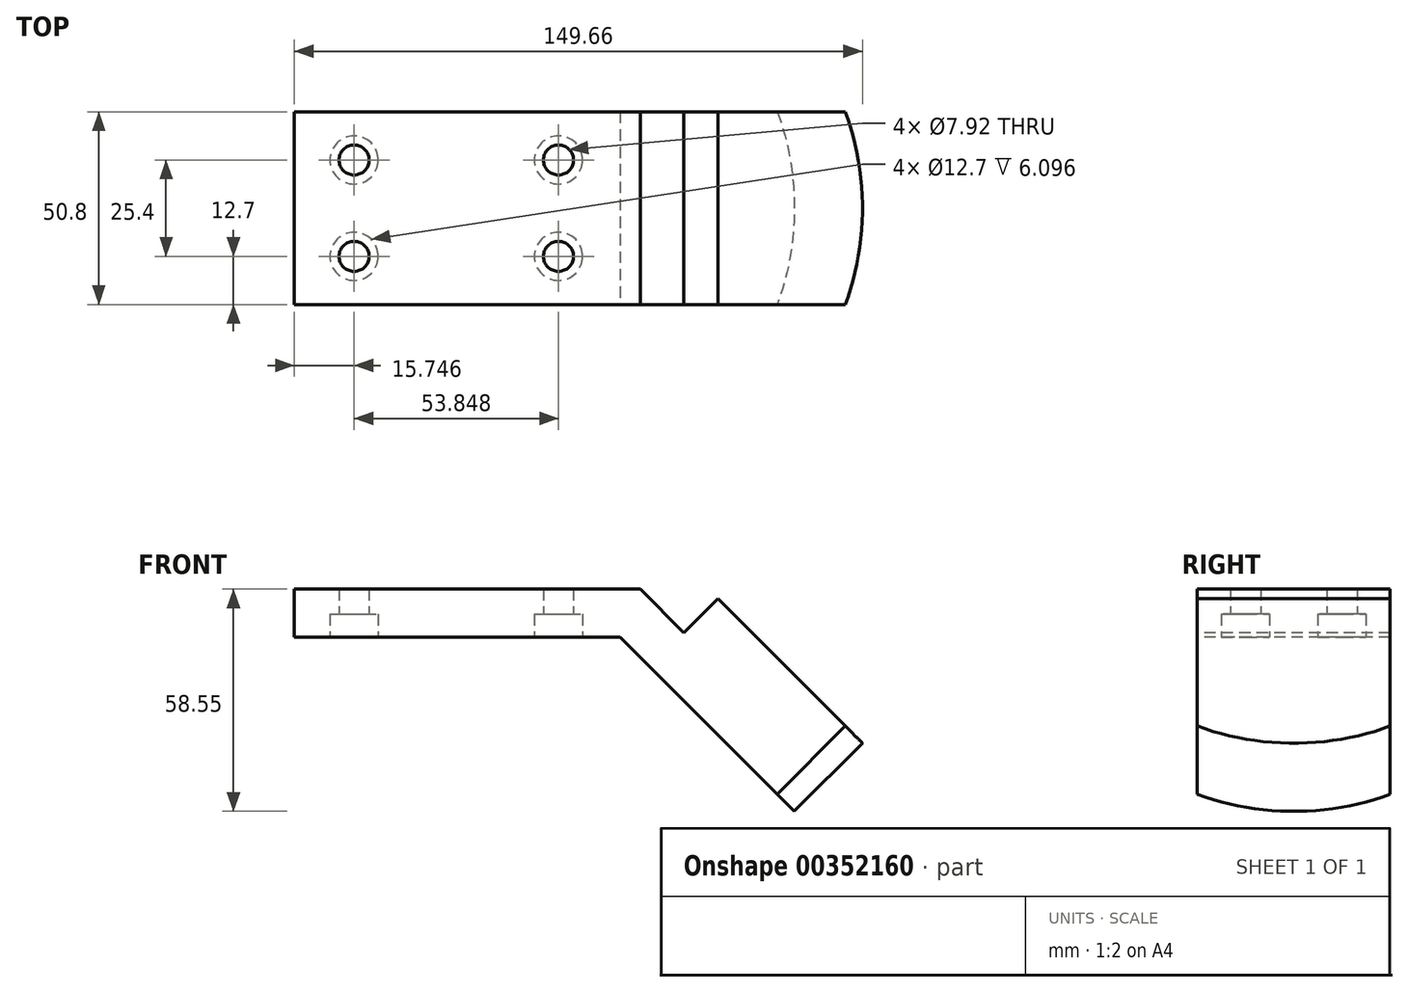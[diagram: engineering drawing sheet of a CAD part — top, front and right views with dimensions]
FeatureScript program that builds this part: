
annotation { "Feature Type Name" : "Feature", "Feature Type Description" : "" }
export const myFeature = defineFeature(function(context is Context, id is Id, definition is map)
    precondition{}
    {
        {
            var Q0;
            Q0=qCreatedBy(makeId("Front.planeOp"),FACE);
            var sketch = newSketch(context, id + "F0", { "sketchPlane" : qUnion([Q0])});
            skLineSegment(sketch, "E0", {"start": v(-17.57, 2.51) * mm, "end": v(-17.57, -10.19) * mm});
            skLineSegment(sketch, "E1", {"start": v(-17.57, -10.19) * mm, "end": v(68.28, -10.19) * mm});
            skLineSegment(sketch, "E2", {"start": v(68.28, -10.19) * mm, "end": v(114.13, -56.04) * mm});
            skLineSegment(sketch, "E3", {"start": v(114.13, -56.04) * mm, "end": v(132.1, -38.08) * mm});
            skLineSegment(sketch, "E4", {"start": v(132.1, -38.08) * mm, "end": v(94.02, 0) * mm});
            skLineSegment(sketch, "E5", {"start": v(94.02, 0) * mm, "end": v(85.04, -8.98) * mm});
            skLineSegment(sketch, "E6", {"start": v(85.04, -8.98) * mm, "end": v(73.54, 2.51) * mm});
            skLineSegment(sketch, "E7", {"start": v(73.54, 2.51) * mm, "end": v(-17.57, 2.51) * mm});
            skSolve(sketch);
        }
        {
            var Q0;
            Q0 = qSketchRegion(id + "F0", true);
            extrude(context, id + "F1", {"entities" : qUnion([Q0]), "oppositeDirection" : true, "depth" : 50.8 * mm});
        }
        {
            var Q0;
            Q0=makeQuery(id+"F1.opExtrude","SWEPT_FACE",FACE,{"disambiguationData":[OSD([sQuery(id+"F0.wireOp",EDGE,"E1")])]});
            cPlane(context, id + "F2", {"entities" : qUnion([Q0]), "cplaneType" : CPlaneType.OFFSET, "offset" : 0 * mm, "width" : 152.4 * mm, "height" : 152.4 * mm});
        }
        {
            var Q0;
            Q0=qCreatedBy(id+"F2.planeOp",FACE);
            var sketch = newSketch(context, id + "F3", { "sketchPlane" : qUnion([Q0])});
            skCircle(sketch, "E8", {"center": v(-1.82, -12.7) * mm, "radius": 3.96 * mm});
            skCircle(sketch, "E9", {"center": v(-1.82, -38.1) * mm, "radius": 3.96 * mm});
            skCircle(sketch, "E10", {"center": v(52.02, -12.7) * mm, "radius": 3.96 * mm});
            skCircle(sketch, "E11", {"center": v(52.02, -38.1) * mm, "radius": 3.96 * mm});
            skSolve(sketch);
        }
        {
            var Q0;
            Q0=sQuery(id+"F3.wireOp",VERTEX,"E8.center");
            var Q1;
            Q1=sQuery(id+"F3.wireOp",VERTEX,"E9.center");
            var Q2;
            Q2=sQuery(id+"F3.wireOp",VERTEX,"E10.center");
            var Q3;
            Q3=sQuery(id+"F3.wireOp",VERTEX,"E11.center");
            var Q4;
            Q4=makeQuery(id+"F1.opExtrude","SWEPT_BODY",BODY,{"disambiguationData":[OSD([sQuery(id+"F0.wireOp",EDGE,"E0"),sQuery(id+"F0.wireOp",EDGE,"E1"),sQuery(id+"F0.wireOp",EDGE,"E2"),sQuery(id+"F0.wireOp",EDGE,"E3"),sQuery(id+"F0.wireOp",EDGE,"E4"),sQuery(id+"F0.wireOp",EDGE,"E5"),sQuery(id+"F0.wireOp",EDGE,"E6"),sQuery(id+"F0.wireOp",EDGE,"E7")])]});
            hole(context, id + "F4", {"style" : HoleStyle.C_BORE, "endStyle" : HoleEndStyle.THROUGH, "holeDiameter" : 7.92 * mm, "cBoreDiameter" : 12.7 * mm, "cBoreDepth" : 6.1 * mm, "isTappedThrough" : true, "tappedDepth" : 12.7 * mm, "tapClearance" : 3, "startFromSketch" : true, "locations" : qUnion([Q0, Q1, Q2, Q3]), "scope" : qUnion([Q4])});
        }
        {
            var Q0;
            Q0=makeQuery(id+"F1.opExtrude","SWEPT_FACE",FACE,{"disambiguationData":[OSD([sQuery(id+"F0.wireOp",EDGE,"E4")])]});
            cPlane(context, id + "F5", {"entities" : qUnion([Q0]), "cplaneType" : CPlaneType.OFFSET, "offset" : 0 * mm, "width" : 152.4 * mm, "height" : 152.4 * mm});
        }
        {
            var Q0;
            Q0=makeQuery(id+"F1.opExtrude","SWEPT_FACE",FACE,{"disambiguationData":[OSD([sQuery(id+"F0.wireOp",EDGE,"E3")])]});
            cPlane(context, id + "F6", {"entities" : qUnion([Q0]), "cplaneType" : CPlaneType.OFFSET, "offset" : 0 * mm, "width" : 152.4 * mm, "height" : 152.4 * mm});
        }
        {
            var Q0;
            Q0=qCreatedBy(id+"F5.planeOp",FACE);
            var sketch = newSketch(context, id + "F7", { "sketchPlane" : qUnion([Q0])});
            skArc(sketch, "E12", {"start": v(0, -113.96) * mm, "mid": v(25.4, -120.33) * mm, "end": v(50.8, -113.96) * mm});
            skLineSegment(sketch, "E13", {"start": v(0, -113.96) * mm, "end": v(0, -123.43) * mm});
            skLineSegment(sketch, "E14", {"start": v(0, -123.43) * mm, "end": v(50.8, -123.43) * mm});
            skLineSegment(sketch, "E15", {"start": v(50.8, -123.43) * mm, "end": v(50.8, -113.96) * mm});
            skSolve(sketch);
        }
        {
            var Q0;
            Q0 = qSketchRegion(id + "F7", true);
            extrude(context, id + "F8", {"entities" : qUnion([Q0]), "operationType" : NewBodyOperationType.REMOVE, "endBound" : BoundingType.THROUGH_ALL, "oppositeDirection" : true, "depth" : 25.4 * mm});
        }
        {
            var Q0;
            Q0=qCreatedBy(id+"F6.planeOp",FACE);
            var sketch = newSketch(context, id + "F9", { "sketchPlane" : qUnion([Q0])});
            skLineSegment(sketch, "E16", {"start": v(66.48, -15.75) * mm, "end": v(60.38, -15.75) * mm});
            skLineSegment(sketch, "E17", {"start": v(60.38, -15.75) * mm, "end": v(60.38, -9.65) * mm});
            skLineSegment(sketch, "E18", {"start": v(60.38, -9.65) * mm, "end": v(53.78, -9.65) * mm});
            skLineSegment(sketch, "E19", {"start": v(53.78, -9.65) * mm, "end": v(53.78, -41.15) * mm});
            skLineSegment(sketch, "E20", {"start": v(53.78, -41.15) * mm, "end": v(60.38, -41.15) * mm});
            skLineSegment(sketch, "E21", {"start": v(60.38, -41.15) * mm, "end": v(60.38, -35.05) * mm});
            skLineSegment(sketch, "E22", {"start": v(60.38, -35.05) * mm, "end": v(66.48, -35.05) * mm});
            skLineSegment(sketch, "E23", {"start": v(66.48, -35.05) * mm, "end": v(66.48, -15.75) * mm});
            skSolve(sketch);
        }
        {
            var Q0;
            Q0 = qSketchRegion(id + "F9", true);
            extrude(context, id + "F10", {"entities" : qUnion([Q0]), "operationType" : NewBodyOperationType.REMOVE, "endBound" : BoundingType.THROUGH_ALL, "oppositeDirection" : true, "depth" : 25.4 * mm});
        }
    });
